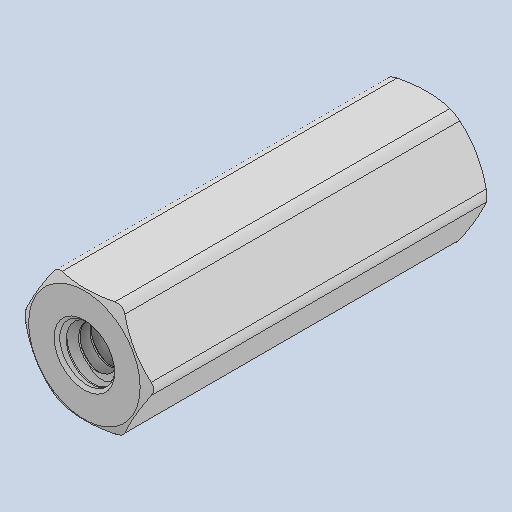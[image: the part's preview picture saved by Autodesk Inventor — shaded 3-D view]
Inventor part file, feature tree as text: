
AUTODESK INVENTOR PART (.ipt)
format: ipt  version: 2023 (Build 270158000, 158)  size: 738,304 bytes
history: native  units: in
note: dims shown in document units (in); Inventor stores cm internally (conversion verified against a paired STEP export)
features: mirror x1
ambient origin geometry x8: Origin, YZ Plane, XZ Plane, XY Plane, X Axis, Y Axis, Z Axis, Center Point
bodies: Solid1 (feature_tree)
feature tree (1):
  mirror  "Mirror1"
